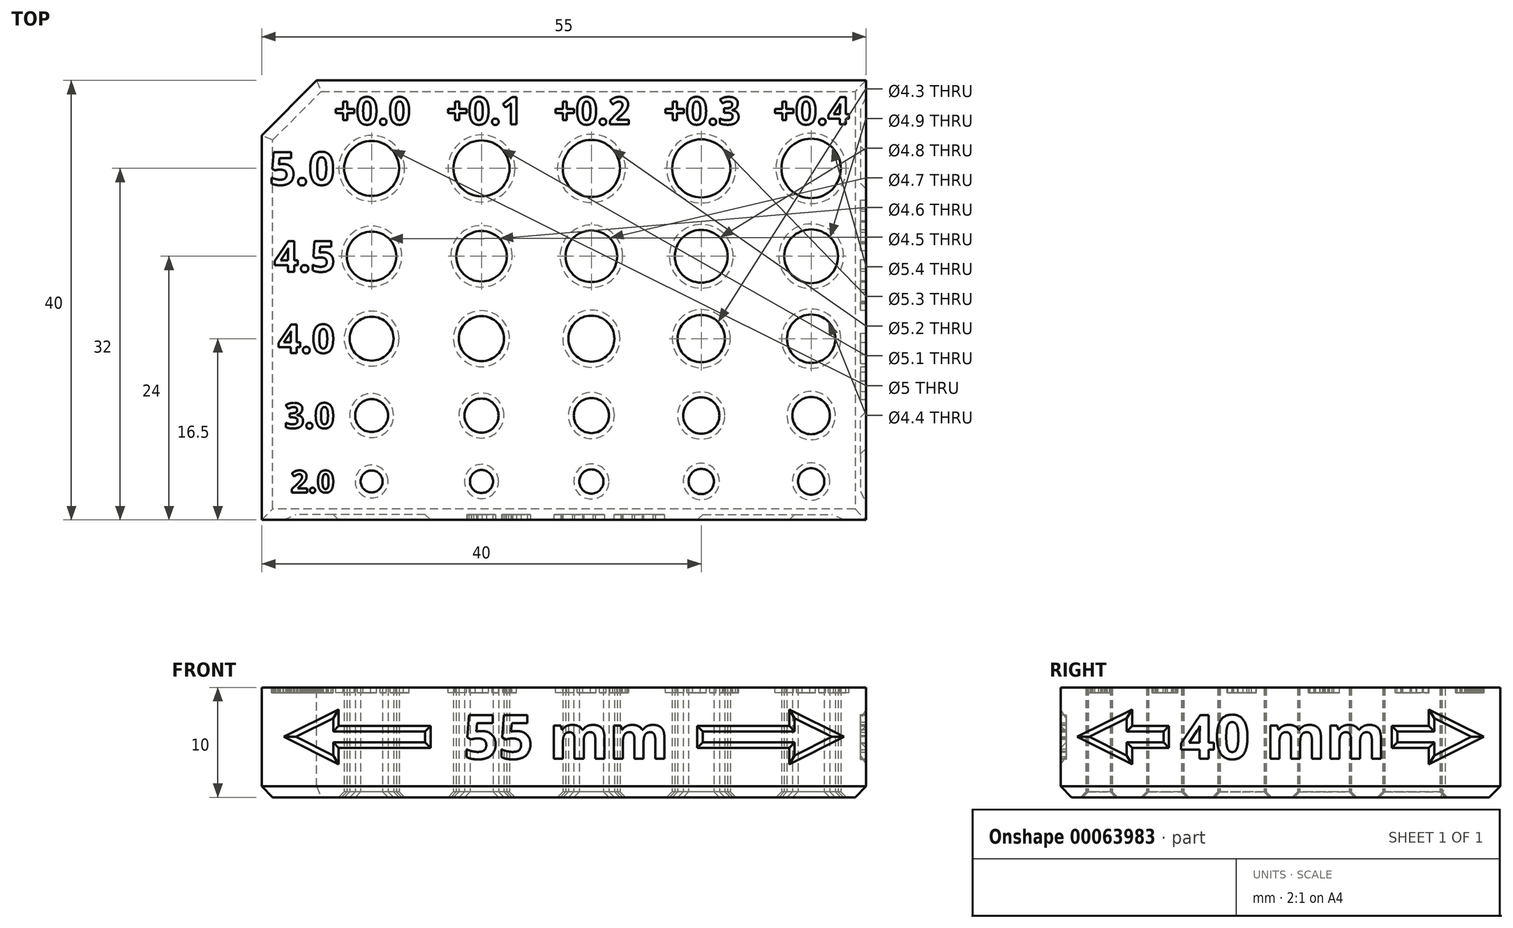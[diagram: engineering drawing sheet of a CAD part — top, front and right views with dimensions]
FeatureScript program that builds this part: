
annotation { "Feature Type Name" : "Feature", "Feature Type Description" : "" }
export const myFeature = defineFeature(function(context is Context, id is Id, definition is map)
    precondition{}
    {
        {
            var Q0;
            Q0=qCreatedBy(makeId("Top.planeOp"),FACE);
            var sketch = newSketch(context, id + "F0", { "sketchPlane" : qUnion([Q0])});
            skLineSegment(sketch, "E0.bottom", {"start": v(0, 0) * mm, "end": v(55, 0) * mm});
            skLineSegment(sketch, "E0.top", {"start": v(0, 40) * mm, "end": v(55, 40) * mm});
            skLineSegment(sketch, "E0.left", {"start": v(0, 0) * mm, "end": v(0, 40) * mm});
            skLineSegment(sketch, "E0.right", {"start": v(55, 0) * mm, "end": v(55, 40) * mm});
            skCircle(sketch, "E1", {"center": v(10, 32) * mm, "radius": 2.5 * mm});
            skCircle(sketch, "E2", {"center": v(20, 32) * mm, "radius": 2.55 * mm});
            skCircle(sketch, "E3", {"center": v(30, 32) * mm, "radius": 2.6 * mm});
            skCircle(sketch, "E4", {"center": v(40, 32) * mm, "radius": 2.65 * mm});
            skCircle(sketch, "E5", {"center": v(50, 32) * mm, "radius": 2.7 * mm});
            skLineSegment(sketch, "E6", {"start": v(50, 32) * mm, "end": v(40, 32) * mm, "construction": true});
            skLineSegment(sketch, "E7", {"start": v(30, 32) * mm, "end": v(40, 32) * mm, "construction": true});
            skLineSegment(sketch, "E8", {"start": v(30, 32) * mm, "end": v(20, 32) * mm, "construction": true});
            skLineSegment(sketch, "E9", {"start": v(20, 32) * mm, "end": v(10, 32) * mm, "construction": true});
            skLineSegment(sketch, "E10", {"start": v(10, 32) * mm, "end": v(0, 32) * mm, "construction": true});
            skLineSegment(sketch, "E11", {"start": v(50, 32) * mm, "end": v(55, 32) * mm, "construction": true});
            skLineSegment(sketch, "E12", {"start": v(10, 32) * mm, "end": v(10, 24) * mm, "construction": true});
            skLineSegment(sketch, "E13", {"start": v(10, 24) * mm, "end": v(20, 24) * mm, "construction": true});
            skLineSegment(sketch, "E14", {"start": v(20, 24) * mm, "end": v(30, 24) * mm, "construction": true});
            skLineSegment(sketch, "E15", {"start": v(30, 24) * mm, "end": v(40, 24) * mm, "construction": true});
            skLineSegment(sketch, "E16", {"start": v(40, 24) * mm, "end": v(50, 24) * mm, "construction": true});
            skLineSegment(sketch, "E17", {"start": v(50, 24) * mm, "end": v(50, 32) * mm, "construction": true});
            skLineSegment(sketch, "E18", {"start": v(40, 24) * mm, "end": v(40, 32) * mm, "construction": true});
            skLineSegment(sketch, "E19", {"start": v(30, 24) * mm, "end": v(30, 32) * mm, "construction": true});
            skLineSegment(sketch, "E20", {"start": v(20, 24) * mm, "end": v(20, 32) * mm, "construction": true});
            skLineSegment(sketch, "E21", {"start": v(10, 24) * mm, "end": v(10, 9.5) * mm, "construction": true});
            skLineSegment(sketch, "E22", {"start": v(10, 9.5) * mm, "end": v(20, 9.5) * mm, "construction": true});
            skLineSegment(sketch, "E23", {"start": v(20, 9.5) * mm, "end": v(30, 9.5) * mm, "construction": true});
            skLineSegment(sketch, "E24", {"start": v(30, 9.5) * mm, "end": v(40, 9.5) * mm, "construction": true});
            skLineSegment(sketch, "E25", {"start": v(40, 9.5) * mm, "end": v(50, 9.5) * mm, "construction": true});
            skLineSegment(sketch, "E26", {"start": v(50, 9.5) * mm, "end": v(50, 24) * mm, "construction": true});
            skLineSegment(sketch, "E27", {"start": v(40, 9.5) * mm, "end": v(40, 24) * mm, "construction": true});
            skLineSegment(sketch, "E28", {"start": v(30, 9.5) * mm, "end": v(30, 24) * mm, "construction": true});
            skLineSegment(sketch, "E29", {"start": v(20, 9.5) * mm, "end": v(20, 24) * mm, "construction": true});
            skCircle(sketch, "E30", {"center": v(10, 24) * mm, "radius": 2.25 * mm});
            skCircle(sketch, "E31", {"center": v(20, 24) * mm, "radius": 2.3 * mm});
            skCircle(sketch, "E32", {"center": v(30, 24) * mm, "radius": 2.35 * mm});
            skCircle(sketch, "E33", {"center": v(40, 24) * mm, "radius": 2.4 * mm});
            skCircle(sketch, "E34", {"center": v(50, 24) * mm, "radius": 2.45 * mm});
            skCircle(sketch, "E35", {"center": v(10, 9.5) * mm, "radius": 1.5 * mm});
            skCircle(sketch, "E36", {"center": v(20, 9.5) * mm, "radius": 1.55 * mm});
            skCircle(sketch, "E37", {"center": v(30, 9.5) * mm, "radius": 1.6 * mm});
            skCircle(sketch, "E38", {"center": v(40, 9.5) * mm, "radius": 1.65 * mm});
            skCircle(sketch, "E39", {"center": v(50, 9.5) * mm, "radius": 1.7 * mm});
            skLineSegment(sketch, "E40", {"start": v(10, 9.5) * mm, "end": v(10, 3.5) * mm, "construction": true});
            skLineSegment(sketch, "E41", {"start": v(10, 3.5) * mm, "end": v(20, 3.5) * mm, "construction": true});
            skLineSegment(sketch, "E42", {"start": v(20, 3.5) * mm, "end": v(30, 3.5) * mm, "construction": true});
            skLineSegment(sketch, "E43", {"start": v(30, 3.5) * mm, "end": v(40, 3.5) * mm, "construction": true});
            skLineSegment(sketch, "E44", {"start": v(40, 3.5) * mm, "end": v(50, 3.5) * mm, "construction": true});
            skLineSegment(sketch, "E45", {"start": v(50, 3.5) * mm, "end": v(50, 9.5) * mm, "construction": true});
            skLineSegment(sketch, "E46", {"start": v(40, 3.5) * mm, "end": v(40, 9.5) * mm, "construction": true});
            skLineSegment(sketch, "E47", {"start": v(30, 3.5) * mm, "end": v(30, 9.5) * mm, "construction": true});
            skLineSegment(sketch, "E48", {"start": v(20, 3.5) * mm, "end": v(20, 9.5) * mm, "construction": true});
            skCircle(sketch, "E49", {"center": v(10, 3.5) * mm, "radius": 1 * mm});
            skCircle(sketch, "E50", {"center": v(20, 3.5) * mm, "radius": 1.05 * mm});
            skCircle(sketch, "E51", {"center": v(30, 3.5) * mm, "radius": 1.1 * mm});
            skCircle(sketch, "E52", {"center": v(40, 3.5) * mm, "radius": 1.15 * mm});
            skCircle(sketch, "E53", {"center": v(50, 3.5) * mm, "radius": 1.2 * mm});
            skLineSegment(sketch, "E54", {"start": v(10, 16.5) * mm, "end": v(20, 16.5) * mm, "construction": true});
            skLineSegment(sketch, "E55", {"start": v(20, 16.5) * mm, "end": v(30, 16.5) * mm, "construction": true});
            skLineSegment(sketch, "E56", {"start": v(30, 16.5) * mm, "end": v(40, 16.5) * mm, "construction": true});
            skLineSegment(sketch, "E57", {"start": v(40, 16.5) * mm, "end": v(50, 16.5) * mm, "construction": true});
            skCircle(sketch, "E58", {"center": v(10, 16.5) * mm, "radius": 2 * mm});
            skCircle(sketch, "E59", {"center": v(20, 16.5) * mm, "radius": 2.05 * mm});
            skCircle(sketch, "E60", {"center": v(30, 16.5) * mm, "radius": 2.1 * mm});
            skCircle(sketch, "E61", {"center": v(40, 16.5) * mm, "radius": 2.15 * mm});
            skCircle(sketch, "E62", {"center": v(50, 16.5) * mm, "radius": 2.2 * mm});
            skSolve(sketch);
        }
        {
            var Q0;
            Q0=makeQuery(id+"F0.imprint","IMPRINT",FACE,{"disambiguationData":[TD([[makeQuery(id+"F0.imprint","IMPRINT",EDGE,{"derivedFrom":sQuery(id+"F0.wireOp",EDGE,"E0.bottom")}),1.0]])]});
            extrude(context, id + "F1", {"entities" : qUnion([Q0]), "depth" : 10 * mm});
        }
        {
            var Q0;
            Q0=makeQuery(id+"F1.opExtrude","CAP_FACE",FACE,{"disambiguationData":[OSD([sQuery(id+"F0.wireOp",EDGE,"E0.bottom"),sQuery(id+"F0.wireOp",EDGE,"E0.top"),sQuery(id+"F0.wireOp",EDGE,"E0.left"),sQuery(id+"F0.wireOp",EDGE,"E0.right"),sQuery(id+"F0.wireOp",EDGE,"E1"),sQuery(id+"F0.wireOp",EDGE,"E2"),sQuery(id+"F0.wireOp",EDGE,"E3"),sQuery(id+"F0.wireOp",EDGE,"E4"),sQuery(id+"F0.wireOp",EDGE,"E5"),sQuery(id+"F0.wireOp",EDGE,"E30"),sQuery(id+"F0.wireOp",EDGE,"E31"),sQuery(id+"F0.wireOp",EDGE,"E32"),sQuery(id+"F0.wireOp",EDGE,"E33"),sQuery(id+"F0.wireOp",EDGE,"E34"),sQuery(id+"F0.wireOp",EDGE,"E35"),sQuery(id+"F0.wireOp",EDGE,"E36"),sQuery(id+"F0.wireOp",EDGE,"E37"),sQuery(id+"F0.wireOp",EDGE,"E38"),sQuery(id+"F0.wireOp",EDGE,"E39"),sQuery(id+"F0.wireOp",EDGE,"E49"),sQuery(id+"F0.wireOp",EDGE,"E50"),sQuery(id+"F0.wireOp",EDGE,"E51"),sQuery(id+"F0.wireOp",EDGE,"E52"),sQuery(id+"F0.wireOp",EDGE,"E53"),sQuery(id+"F0.wireOp",EDGE,"E58"),sQuery(id+"F0.wireOp",EDGE,"E59"),sQuery(id+"F0.wireOp",EDGE,"E60"),sQuery(id+"F0.wireOp",EDGE,"E61"),sQuery(id+"F0.wireOp",EDGE,"E62")])],"isStart":false});
            var sketch = newSketch(context, id + "F2", { "sketchPlane" : qUnion([Q0])});
            skText(sketch, "E63", { "text": "+0.0", "fontName": "OpenSans-Bold.ttf"});
            skText(sketch, "E64", { "text": "+0.1", "fontName": "OpenSans-Bold.ttf"});
            skText(sketch, "E65", { "text": "+0.2", "fontName": "OpenSans-Bold.ttf"});
            skText(sketch, "E66", { "text": "+0.3", "fontName": "OpenSans-Bold.ttf"});
            skText(sketch, "E67", { "text": "+0.4", "fontName": "OpenSans-Bold.ttf"});
            skLineSegment(sketch, "E68", {"start": v(13.4, 38.5) * mm, "end": v(16.8, 38.5) * mm, "construction": true});
            skLineSegment(sketch, "E69", {"start": v(23.2, 38.5) * mm, "end": v(26.59, 38.5) * mm, "construction": true});
            skLineSegment(sketch, "E70", {"start": v(33.41, 38.5) * mm, "end": v(36.6, 38.5) * mm, "construction": true});
            skLineSegment(sketch, "E71", {"start": v(43.4, 38.5) * mm, "end": v(46.56, 38.5) * mm, "construction": true});
            skLineSegment(sketch, "E72", {"start": v(46.56, 36) * mm, "end": v(43.4, 36) * mm, "construction": true});
            skLineSegment(sketch, "E73", {"start": v(36.6, 36) * mm, "end": v(33.41, 36) * mm, "construction": true});
            skLineSegment(sketch, "E74", {"start": v(26.59, 36) * mm, "end": v(23.2, 36) * mm, "construction": true});
            skLineSegment(sketch, "E75", {"start": v(16.8, 36) * mm, "end": v(13.4, 36) * mm, "construction": true});
            skLineSegment(sketch, "E76", {"start": v(10, 32) * mm, "end": v(10, 36) * mm, "construction": true});
            skLineSegment(sketch, "E77", {"start": v(20, 36) * mm, "end": v(20, 32) * mm, "construction": true});
            skLineSegment(sketch, "E78", {"start": v(30, 32) * mm, "end": v(30, 36) * mm, "construction": true});
            skLineSegment(sketch, "E79", {"start": v(40, 36) * mm, "end": v(40, 32) * mm, "construction": true});
            skLineSegment(sketch, "E80", {"start": v(50, 32) * mm, "end": v(50, 36) * mm, "construction": true});
            skText(sketch, "E81", { "text": "5.0", "fontName": "OpenSans-Bold.ttf"});
            skText(sketch, "E82", { "text": "4.5", "fontName": "OpenSans-Bold.ttf"});
            skText(sketch, "E83", { "text": "4.0", "fontName": "OpenSans-Bold.ttf"});
            skText(sketch, "E84", { "text": "3.0", "fontName": "OpenSans-Bold.ttf"});
            skText(sketch, "E85", { "text": "2.0", "fontName": "OpenSans-Bold.ttf"});
            skLineSegment(sketch, "E86", {"start": v(6.5, 30.5) * mm, "end": v(6.5, 25.4) * mm, "construction": true});
            skLineSegment(sketch, "E87", {"start": v(6.5, 22.6) * mm, "end": v(6.5, 17.8) * mm, "construction": true});
            skLineSegment(sketch, "E88", {"start": v(6.5, 15.2) * mm, "end": v(6.5, 10.65) * mm, "construction": true});
            skLineSegment(sketch, "E89", {"start": v(6.5, 8.35) * mm, "end": v(6.5, 4.5) * mm, "construction": true});
            skLineSegment(sketch, "E90", {"start": v(6.5, 32) * mm, "end": v(10, 32) * mm, "construction": true});
            skLineSegment(sketch, "E91", {"start": v(6.5, 24) * mm, "end": v(10, 24) * mm, "construction": true});
            skLineSegment(sketch, "E92", {"start": v(6.5, 16.5) * mm, "end": v(10, 16.5) * mm, "construction": true});
            skLineSegment(sketch, "E93", {"start": v(6.5, 9.5) * mm, "end": v(10, 9.5) * mm, "construction": true});
            skLineSegment(sketch, "E94", {"start": v(6.5, 3.5) * mm, "end": v(10, 3.5) * mm, "construction": true});
            const initialGuessF2  = {"E63": [0.0066, 0.036, 1, 0, 0.0025], "E64": [0.0168, 0.036, 1, 0, 0.0025], "E65": [0.02659, 0.036, 1, 0, 0.0025], "E66": [0.0366, 0.036, 1, 0, 0.0025], "E67": [0.04656, 0.036, 1, 0, 0.0025], "E81": [0.0007, 0.0305, 1, 0, 0.003], "E82": [0.00113, 0.0226, 1, 0, 0.0028], "E83": [0.00148, 0.0152, 1, 0, 0.0026], "E84": [0.00206, 0.00835, 1, 0, 0.0023], "E85": [0.00264, 0.0025, 1, 0, 0.002]};
            skSetInitialGuess(sketch, initialGuessF2);
            skSolve(sketch);
        }
        {
            var Q0;
            Q0 = qSketchRegion(id + "F2", true);
            extrude(context, id + "F3", {"entities" : qUnion([Q0]), "operationType" : NewBodyOperationType.REMOVE, "oppositeDirection" : true, "depth" : .5 * mm});
        }
        {
            var Q0;
            Q0=makeQuery(id+"F1.opExtrude","SWEPT_EDGE",EDGE,{"disambiguationData":[OSD([sQuery(id+"F0.wireOp",EDGE,"E0.top"),sQuery(id+"F0.wireOp",EDGE,"E0.left")])]});
            chamfer(context, id + "F4", {"entities" : qUnion([Q0]), "width" : 5 * mm, "tangentPropagation" : true});
        }
        {
            var Q0;
            Q0=makeQuery(id+"F1.opExtrude","CAP_EDGE",EDGE,{"disambiguationData":[OSD([sQuery(id+"F0.wireOp",EDGE,"E0.bottom")])],"isStart":true});
            var Q1;
            Q1=makeQuery(id+"F1.opExtrude","CAP_EDGE",EDGE,{"disambiguationData":[OSD([sQuery(id+"F0.wireOp",EDGE,"E0.left")])],"isStart":true});
            var Q2;
            Q2=makeQuery(id+"F1.opExtrude","CAP_EDGE",EDGE,{"disambiguationData":[OSD([sQuery(id+"F0.wireOp",EDGE,"E0.top")])],"isStart":true});
            var Q3;
            Q3=makeQuery(id+"F1.opExtrude","CAP_EDGE",EDGE,{"disambiguationData":[OSD([sQuery(id+"F0.wireOp",EDGE,"E0.right")])],"isStart":true});
            var Q4;
            {var subQ0=sQuery(id+"F0.wireOp",EDGE,"E0.left");var subQ1=sQuery(id+"F0.wireOp",EDGE,"E0.top");Q4=makeQuery(id+"F4.opChamfer","BLEND_EDGE",EDGE,{"blendedFrom":[makeQuery(id+"F1.opExtrude","SWEPT_EDGE",EDGE,{"disambiguationData":[OSD([subQ1,subQ0])]}),makeQuery(id+"F1.opExtrude","CAP_FACE",FACE,{"disambiguationData":[OSD([sQuery(id+"F0.wireOp",EDGE,"E0.bottom"),subQ1,subQ0,sQuery(id+"F0.wireOp",EDGE,"E0.right"),sQuery(id+"F0.wireOp",EDGE,"E1"),sQuery(id+"F0.wireOp",EDGE,"E2"),sQuery(id+"F0.wireOp",EDGE,"E3"),sQuery(id+"F0.wireOp",EDGE,"E4"),sQuery(id+"F0.wireOp",EDGE,"E5"),sQuery(id+"F0.wireOp",EDGE,"E30"),sQuery(id+"F0.wireOp",EDGE,"E31"),sQuery(id+"F0.wireOp",EDGE,"E32"),sQuery(id+"F0.wireOp",EDGE,"E33"),sQuery(id+"F0.wireOp",EDGE,"E34"),sQuery(id+"F0.wireOp",EDGE,"E35"),sQuery(id+"F0.wireOp",EDGE,"E36"),sQuery(id+"F0.wireOp",EDGE,"E37"),sQuery(id+"F0.wireOp",EDGE,"E38"),sQuery(id+"F0.wireOp",EDGE,"E39"),sQuery(id+"F0.wireOp",EDGE,"E49"),sQuery(id+"F0.wireOp",EDGE,"E50"),sQuery(id+"F0.wireOp",EDGE,"E51"),sQuery(id+"F0.wireOp",EDGE,"E52"),sQuery(id+"F0.wireOp",EDGE,"E53"),sQuery(id+"F0.wireOp",EDGE,"E58"),sQuery(id+"F0.wireOp",EDGE,"E59"),sQuery(id+"F0.wireOp",EDGE,"E60"),sQuery(id+"F0.wireOp",EDGE,"E61"),sQuery(id+"F0.wireOp",EDGE,"E62")])],"isStart":true})],"blendedInto":[makeQuery(id+"F1.opExtrude","CAP_FACE",FACE,{"disambiguationData":[OSD([sQuery(id+"F0.wireOp",EDGE,"E0.bottom"),subQ1,subQ0,sQuery(id+"F0.wireOp",EDGE,"E0.right"),sQuery(id+"F0.wireOp",EDGE,"E1"),sQuery(id+"F0.wireOp",EDGE,"E2"),sQuery(id+"F0.wireOp",EDGE,"E3"),sQuery(id+"F0.wireOp",EDGE,"E4"),sQuery(id+"F0.wireOp",EDGE,"E5"),sQuery(id+"F0.wireOp",EDGE,"E30"),sQuery(id+"F0.wireOp",EDGE,"E31"),sQuery(id+"F0.wireOp",EDGE,"E32"),sQuery(id+"F0.wireOp",EDGE,"E33"),sQuery(id+"F0.wireOp",EDGE,"E34"),sQuery(id+"F0.wireOp",EDGE,"E35"),sQuery(id+"F0.wireOp",EDGE,"E36"),sQuery(id+"F0.wireOp",EDGE,"E37"),sQuery(id+"F0.wireOp",EDGE,"E38"),sQuery(id+"F0.wireOp",EDGE,"E39"),sQuery(id+"F0.wireOp",EDGE,"E49"),sQuery(id+"F0.wireOp",EDGE,"E50"),sQuery(id+"F0.wireOp",EDGE,"E51"),sQuery(id+"F0.wireOp",EDGE,"E52"),sQuery(id+"F0.wireOp",EDGE,"E53"),sQuery(id+"F0.wireOp",EDGE,"E58"),sQuery(id+"F0.wireOp",EDGE,"E59"),sQuery(id+"F0.wireOp",EDGE,"E60"),sQuery(id+"F0.wireOp",EDGE,"E61"),sQuery(id+"F0.wireOp",EDGE,"E62")])],"isStart":true})]});}
            chamfer(context, id + "F5", {"entities" : qUnion([Q0, Q1, Q2, Q3, Q4]), "width" : 1 * mm, "tangentPropagation" : true});
        }
        {
            var Q0;
            Q0=makeQuery(id+"F1.opExtrude","SWEPT_FACE",FACE,{"disambiguationData":[OSD([sQuery(id+"F0.wireOp",EDGE,"E0.bottom")])]});
            var sketch = newSketch(context, id + "F6", { "sketchPlane" : qUnion([Q0])});
            skText(sketch, "E95", { "text": "55 mm", "fontName": "OpenSans-Bold.ttf"});
            skLineSegment(sketch, "E96", {"start": v(27.5, 10) * mm, "end": v(27.5, 7.5) * mm, "construction": true});
            skLineSegment(sketch, "E97", {"start": v(36.64, 5.5) * mm, "end": v(55, 5.5) * mm, "construction": true});
            skLineSegment(sketch, "E98", {"start": v(18.36, 5.5) * mm, "end": v(0, 5.5) * mm, "construction": true});
            skLineSegment(sketch, "E99", {"start": v(39.64, 5.5) * mm, "end": v(39.64, 6.5) * mm});
            skLineSegment(sketch, "E100", {"start": v(39.64, 6.5) * mm, "end": v(48, 6.5) * mm});
            skLineSegment(sketch, "E101", {"start": v(48, 6.5) * mm, "end": v(48, 8) * mm});
            skLineSegment(sketch, "E102", {"start": v(48, 8) * mm, "end": v(53, 5.5) * mm});
            skLineSegment(sketch, "E103.MirrorCS", {"start": v(39.64, 5.5) * mm, "end": v(39.64, 4.5) * mm});
            skLineSegment(sketch, "E104.MirrorCS", {"start": v(39.64, 4.5) * mm, "end": v(48, 4.5) * mm});
            skLineSegment(sketch, "E105.MirrorCS", {"start": v(48, 4.5) * mm, "end": v(48, 3) * mm});
            skLineSegment(sketch, "E106.MirrorCS", {"start": v(48, 3) * mm, "end": v(53, 5.5) * mm});
            skLineSegment(sketch, "E107.MirrorCS", {"start": v(15.36, 6.5) * mm, "end": v(7, 6.5) * mm});
            skLineSegment(sketch, "E108.MirrorCS", {"start": v(7, 6.5) * mm, "end": v(7, 8) * mm});
            skLineSegment(sketch, "E109.MirrorCS", {"start": v(7, 8) * mm, "end": v(2, 5.5) * mm});
            skLineSegment(sketch, "E110.MirrorCS", {"start": v(7, 3) * mm, "end": v(2, 5.5) * mm});
            skLineSegment(sketch, "E111.MirrorCS", {"start": v(7, 4.5) * mm, "end": v(7, 3) * mm});
            skLineSegment(sketch, "E112.MirrorCS", {"start": v(15.36, 4.5) * mm, "end": v(7, 4.5) * mm});
            skLineSegment(sketch, "E113.MirrorCS", {"start": v(15.36, 5.5) * mm, "end": v(15.36, 4.5) * mm});
            skLineSegment(sketch, "E114.MirrorCS", {"start": v(15.36, 5.5) * mm, "end": v(15.36, 6.5) * mm});
            const initialGuessF6  = {"E95": [0.01836, 0.0035, 1, 0, 0.004]};
            skSetInitialGuess(sketch, initialGuessF6);
            skSolve(sketch);
        }
        {
            var Q0;
            Q0 = qSketchRegion(id + "F6", true);
            extrude(context, id + "F7", {"entities" : qUnion([Q0]), "operationType" : NewBodyOperationType.REMOVE, "oppositeDirection" : true, "depth" : 0.5 * mm});
        }
        {
            var Q0;
            Q0=makeQuery(id+"F1.opExtrude","SWEPT_FACE",FACE,{"disambiguationData":[OSD([sQuery(id+"F0.wireOp",EDGE,"E0.right")])]});
            var sketch = newSketch(context, id + "F8", { "sketchPlane" : qUnion([Q0])});
            skText(sketch, "E115", { "text": "40 mm", "fontName": "OpenSans-Bold.ttf"});
            skLineSegment(sketch, "E116", {"start": v(10.86, 5.5) * mm, "end": v(0, 5.5) * mm, "construction": true});
            skLineSegment(sketch, "E117", {"start": v(20, 7.5) * mm, "end": v(20, 10) * mm, "construction": true});
            skLineSegment(sketch, "E118", {"start": v(1.5, 5.5) * mm, "end": v(6.5, 8) * mm});
            skLineSegment(sketch, "E119", {"start": v(6.5, 8) * mm, "end": v(6.5, 6.5) * mm});
            skLineSegment(sketch, "E120", {"start": v(6.5, 6.5) * mm, "end": v(9.86, 6.5) * mm});
            skLineSegment(sketch, "E121", {"start": v(9.86, 6.5) * mm, "end": v(9.86, 5.5) * mm});
            skLineSegment(sketch, "E122.MirrorCS", {"start": v(9.86, 4.5) * mm, "end": v(9.86, 5.5) * mm});
            skLineSegment(sketch, "E123.MirrorCS", {"start": v(6.5, 4.5) * mm, "end": v(9.86, 4.5) * mm});
            skLineSegment(sketch, "E124.MirrorCS", {"start": v(6.5, 3) * mm, "end": v(6.5, 4.5) * mm});
            skLineSegment(sketch, "E125.MirrorCS", {"start": v(1.5, 5.5) * mm, "end": v(6.5, 3) * mm});
            skLineSegment(sketch, "E126.MirrorCS", {"start": v(33.5, 8) * mm, "end": v(33.5, 6.5) * mm});
            skLineSegment(sketch, "E127.MirrorCS", {"start": v(33.5, 6.5) * mm, "end": v(30.14, 6.5) * mm});
            skLineSegment(sketch, "E128.MirrorCS", {"start": v(30.14, 6.5) * mm, "end": v(30.14, 5.5) * mm});
            skLineSegment(sketch, "E129.MirrorCS", {"start": v(30.14, 4.5) * mm, "end": v(30.14, 5.5) * mm});
            skLineSegment(sketch, "E130.MirrorCS", {"start": v(33.5, 4.5) * mm, "end": v(30.14, 4.5) * mm});
            skLineSegment(sketch, "E131.MirrorCS", {"start": v(33.5, 3) * mm, "end": v(33.5, 4.5) * mm});
            skLineSegment(sketch, "E132.MirrorCS", {"start": v(38.5, 5.5) * mm, "end": v(33.5, 3) * mm});
            skLineSegment(sketch, "E133.MirrorCS", {"start": v(38.5, 5.5) * mm, "end": v(33.5, 8) * mm});
            const initialGuessF8  = {"E115": [0.01086, 0.0035, 1, 0, 0.004]};
            skSetInitialGuess(sketch, initialGuessF8);
            skSolve(sketch);
        }
        {
            var Q0;
            Q0 = qSketchRegion(id + "F8", true);
            extrude(context, id + "F9", {"entities" : qUnion([Q0]), "operationType" : NewBodyOperationType.REMOVE, "oppositeDirection" : true, "depth" : .5 * mm});
        }
        {
            var Q0;
            Q0=makeQuery(id+"F7.boolean.opBoolean","COPY",FACE,{"derivedFrom":makeQuery(id+"F7.opExtrude","CAP_FACE",FACE,{"disambiguationData":[OSD([sQuery(id+"F6.wireOp",EDGE,"E107.MirrorCS"),sQuery(id+"F6.wireOp",EDGE,"E108.MirrorCS"),sQuery(id+"F6.wireOp",EDGE,"E109.MirrorCS"),sQuery(id+"F6.wireOp",EDGE,"E110.MirrorCS"),sQuery(id+"F6.wireOp",EDGE,"E111.MirrorCS"),sQuery(id+"F6.wireOp",EDGE,"E112.MirrorCS"),sQuery(id+"F6.wireOp",EDGE,"E113.MirrorCS"),sQuery(id+"F6.wireOp",EDGE,"E114.MirrorCS")])],"isStart":false})});
            var Q1;
            Q1=makeQuery(id+"F7.boolean.opBoolean","COPY",FACE,{"derivedFrom":makeQuery(id+"F7.opExtrude","CAP_FACE",FACE,{"disambiguationData":[OSD([sQuery(id+"F6.wireOp",EDGE,"E99"),sQuery(id+"F6.wireOp",EDGE,"E100"),sQuery(id+"F6.wireOp",EDGE,"E101"),sQuery(id+"F6.wireOp",EDGE,"E102"),sQuery(id+"F6.wireOp",EDGE,"E103.MirrorCS"),sQuery(id+"F6.wireOp",EDGE,"E104.MirrorCS"),sQuery(id+"F6.wireOp",EDGE,"E105.MirrorCS"),sQuery(id+"F6.wireOp",EDGE,"E106.MirrorCS")])],"isStart":false})});
            var Q2;
            Q2=makeQuery(id+"F9.boolean.opBoolean","COPY",FACE,{"derivedFrom":makeQuery(id+"F9.opExtrude","CAP_FACE",FACE,{"disambiguationData":[OSD([sQuery(id+"F8.wireOp",EDGE,"E118"),sQuery(id+"F8.wireOp",EDGE,"E119"),sQuery(id+"F8.wireOp",EDGE,"E120"),sQuery(id+"F8.wireOp",EDGE,"E121"),sQuery(id+"F8.wireOp",EDGE,"E122.MirrorCS"),sQuery(id+"F8.wireOp",EDGE,"E123.MirrorCS"),sQuery(id+"F8.wireOp",EDGE,"E124.MirrorCS"),sQuery(id+"F8.wireOp",EDGE,"E125.MirrorCS")])],"isStart":false})});
            var Q3;
            Q3=makeQuery(id+"F9.boolean.opBoolean","COPY",FACE,{"derivedFrom":makeQuery(id+"F9.opExtrude","CAP_FACE",FACE,{"disambiguationData":[OSD([sQuery(id+"F8.wireOp",EDGE,"E126.MirrorCS"),sQuery(id+"F8.wireOp",EDGE,"E127.MirrorCS"),sQuery(id+"F8.wireOp",EDGE,"E128.MirrorCS"),sQuery(id+"F8.wireOp",EDGE,"E129.MirrorCS"),sQuery(id+"F8.wireOp",EDGE,"E130.MirrorCS"),sQuery(id+"F8.wireOp",EDGE,"E131.MirrorCS"),sQuery(id+"F8.wireOp",EDGE,"E132.MirrorCS"),sQuery(id+"F8.wireOp",EDGE,"E133.MirrorCS")])],"isStart":false})});
            chamfer(context, id + "F10", {"entities" : qUnion([Q0, Q1, Q2, Q3]), "width" : .5 * mm, "tangentPropagation" : true});
        }
        {
            var Q0;
            Q0=makeQuery(id+"F1.opExtrude","CAP_EDGE",EDGE,{"disambiguationData":[OSD([sQuery(id+"F0.wireOp",EDGE,"E2")])],"isStart":true});
            var Q1;
            Q1=makeQuery(id+"F1.opExtrude","CAP_EDGE",EDGE,{"disambiguationData":[OSD([sQuery(id+"F0.wireOp",EDGE,"E31")])],"isStart":true});
            var Q2;
            Q2=makeQuery(id+"F1.opExtrude","CAP_EDGE",EDGE,{"disambiguationData":[OSD([sQuery(id+"F0.wireOp",EDGE,"E59")])],"isStart":true});
            var Q3;
            Q3=makeQuery(id+"F1.opExtrude","CAP_EDGE",EDGE,{"disambiguationData":[OSD([sQuery(id+"F0.wireOp",EDGE,"E36")])],"isStart":true});
            var Q4;
            Q4=makeQuery(id+"F1.opExtrude","CAP_EDGE",EDGE,{"disambiguationData":[OSD([sQuery(id+"F0.wireOp",EDGE,"E50")])],"isStart":true});
            var Q5;
            Q5=makeQuery(id+"F1.opExtrude","CAP_EDGE",EDGE,{"disambiguationData":[OSD([sQuery(id+"F0.wireOp",EDGE,"E49")])],"isStart":true});
            var Q6;
            Q6=makeQuery(id+"F1.opExtrude","CAP_EDGE",EDGE,{"disambiguationData":[OSD([sQuery(id+"F0.wireOp",EDGE,"E35")])],"isStart":true});
            var Q7;
            Q7=makeQuery(id+"F1.opExtrude","CAP_EDGE",EDGE,{"disambiguationData":[OSD([sQuery(id+"F0.wireOp",EDGE,"E58")])],"isStart":true});
            var Q8;
            Q8=makeQuery(id+"F1.opExtrude","CAP_EDGE",EDGE,{"disambiguationData":[OSD([sQuery(id+"F0.wireOp",EDGE,"E30")])],"isStart":true});
            var Q9;
            Q9=makeQuery(id+"F1.opExtrude","CAP_EDGE",EDGE,{"disambiguationData":[OSD([sQuery(id+"F0.wireOp",EDGE,"E1")])],"isStart":true});
            var Q10;
            Q10=makeQuery(id+"F1.opExtrude","CAP_EDGE",EDGE,{"disambiguationData":[OSD([sQuery(id+"F0.wireOp",EDGE,"E3")])],"isStart":true});
            var Q11;
            Q11=makeQuery(id+"F1.opExtrude","CAP_EDGE",EDGE,{"disambiguationData":[OSD([sQuery(id+"F0.wireOp",EDGE,"E32")])],"isStart":true});
            var Q12;
            Q12=makeQuery(id+"F1.opExtrude","CAP_EDGE",EDGE,{"disambiguationData":[OSD([sQuery(id+"F0.wireOp",EDGE,"E60")])],"isStart":true});
            var Q13;
            Q13=makeQuery(id+"F1.opExtrude","CAP_EDGE",EDGE,{"disambiguationData":[OSD([sQuery(id+"F0.wireOp",EDGE,"E37")])],"isStart":true});
            var Q14;
            Q14=makeQuery(id+"F1.opExtrude","CAP_EDGE",EDGE,{"disambiguationData":[OSD([sQuery(id+"F0.wireOp",EDGE,"E51")])],"isStart":true});
            var Q15;
            Q15=makeQuery(id+"F1.opExtrude","CAP_EDGE",EDGE,{"disambiguationData":[OSD([sQuery(id+"F0.wireOp",EDGE,"E52")])],"isStart":true});
            var Q16;
            Q16=makeQuery(id+"F1.opExtrude","CAP_EDGE",EDGE,{"disambiguationData":[OSD([sQuery(id+"F0.wireOp",EDGE,"E38")])],"isStart":true});
            var Q17;
            Q17=makeQuery(id+"F1.opExtrude","CAP_EDGE",EDGE,{"disambiguationData":[OSD([sQuery(id+"F0.wireOp",EDGE,"E61")])],"isStart":true});
            var Q18;
            Q18=makeQuery(id+"F1.opExtrude","CAP_EDGE",EDGE,{"disambiguationData":[OSD([sQuery(id+"F0.wireOp",EDGE,"E33")])],"isStart":true});
            var Q19;
            Q19=makeQuery(id+"F1.opExtrude","CAP_EDGE",EDGE,{"disambiguationData":[OSD([sQuery(id+"F0.wireOp",EDGE,"E4")])],"isStart":true});
            var Q20;
            Q20=makeQuery(id+"F1.opExtrude","CAP_EDGE",EDGE,{"disambiguationData":[OSD([sQuery(id+"F0.wireOp",EDGE,"E5")])],"isStart":true});
            var Q21;
            Q21=makeQuery(id+"F1.opExtrude","CAP_EDGE",EDGE,{"disambiguationData":[OSD([sQuery(id+"F0.wireOp",EDGE,"E34")])],"isStart":true});
            var Q22;
            Q22=makeQuery(id+"F1.opExtrude","CAP_EDGE",EDGE,{"disambiguationData":[OSD([sQuery(id+"F0.wireOp",EDGE,"E62")])],"isStart":true});
            var Q23;
            Q23=makeQuery(id+"F1.opExtrude","CAP_EDGE",EDGE,{"disambiguationData":[OSD([sQuery(id+"F0.wireOp",EDGE,"E39")])],"isStart":true});
            var Q24;
            Q24=makeQuery(id+"F1.opExtrude","CAP_EDGE",EDGE,{"disambiguationData":[OSD([sQuery(id+"F0.wireOp",EDGE,"E53")])],"isStart":true});
            chamfer(context, id + "F11", {"entities" : qUnion([Q0, Q1, Q2, Q3, Q4, Q5, Q6, Q7, Q8, Q9, Q10, Q11, Q12, Q13, Q14, Q15, Q16, Q17, Q18, Q19, Q20, Q21, Q22, Q23, Q24]), "width" : .5 * mm, "tangentPropagation" : true});
        }
    });
